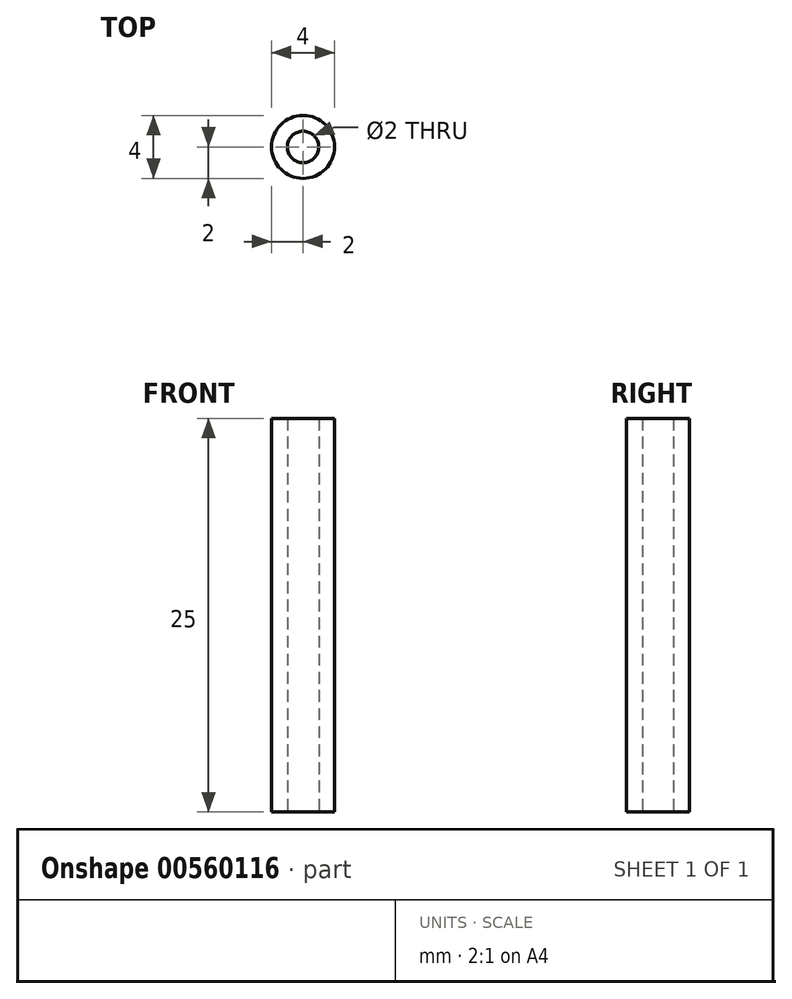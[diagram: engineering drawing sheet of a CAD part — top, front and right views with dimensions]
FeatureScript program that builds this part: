
annotation { "Feature Type Name" : "Feature", "Feature Type Description" : "" }
export const myFeature = defineFeature(function(context is Context, id is Id, definition is map)
    precondition{}
    {
        {
            var Q0;
            Q0=qCreatedBy(makeId("Top.planeOp"),FACE);
            var sketch = newSketch(context, id + "F0", { "sketchPlane" : qUnion([Q0])});
            skCircle(sketch, "E0", {"center": v(0, 0) * mm, "radius": 2 * mm});
            skCircle(sketch, "E1", {"center": v(0, 0) * mm, "radius": 1 * mm});
            skSolve(sketch);
        }
        {
            var Q0;
            Q0=makeQuery(id+"F0.imprint","IMPRINT",FACE,{"disambiguationData":[TD([[makeQuery(id+"F0.imprint","IMPRINT",EDGE,{"derivedFrom":sQuery(id+"F0.wireOp",EDGE,"E0")}),1.0]])]});
            extrude(context, id + "F1", {"entities" : qUnion([Q0]), "depth" : 25 * mm, "offsetDistance" : 25 * mm});
        }
    });
